# Revit family: RBA BIM - RBA1055 Series
name_source: partatom
category: Plumbing Fixtures
revit_build: Autodesk Revit 2014 (Build: 20130308_1515(x64)
units: mm (PartAtom-declared; Revit-internal decimal feet)

## types (2) — shared parameters
Finish = Polished Chrome Finish
Inlet = Inlet 20mm (3/4 inch) BSP
Manufacturer = DOCOL
Material = DZR Brass
Outlet = Outlet 20mm (3/4 inch) BSP
Radius = 20 mm  [stored 0.0656168 ft]
Specifier = RBA Group
URL = www.rba.com.au/tapware/wall-mounted
Vent Connection = No
Waste Connection = No

## per-type parameters (varying)
| type | Description | Model |
| RBA1055-510 (10 second run-time) | Self Closing Tap Valve (10 Second Run-Time) | RBA1055-510 |
| RBA1055-530 (30 second run-time) | Self Closing Tap Valve (30 Second Run-Time) | RBA1055-530 |

note: [stored X ft] marks values corroborated as IEEE doubles in the binary element streams (Revit-internal decimal feet)

## geometry (parser evidence)
native form markers: Sweep x3
no freeform markers — native parametric forms only
